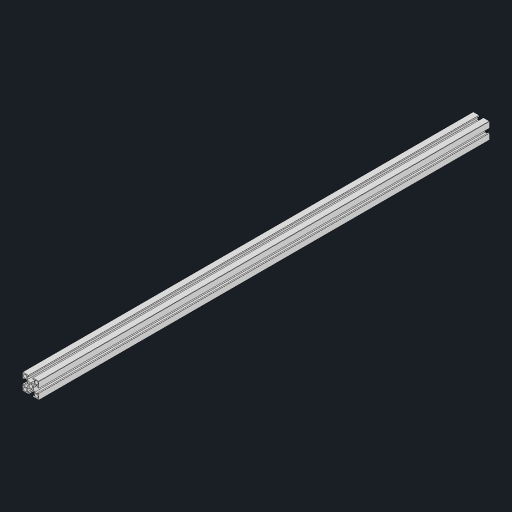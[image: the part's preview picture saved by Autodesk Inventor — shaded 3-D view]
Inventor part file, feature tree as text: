
AUTODESK INVENTOR PART (.ipt)
format: ipt  version: 2024.2 (Build 282272000, 272)  size: 319,488 bytes
history: native  units: mm
features: other x1, extrude x1, fillet x1, sketch x1
ambient origin geometry x8: Origin, YZ Plane, XZ Plane, XY Plane, X Axis, Y Axis, Z Axis, Center Point
bodies: Body1 (feature_tree)
feature tree (4):
  other  "솔리드1"
  extrude  "프로파일 길이 설정"  Depth=20.0mm
  fillet  "모서리"  Radius=20.0mm
  sketch  "스케치1"
